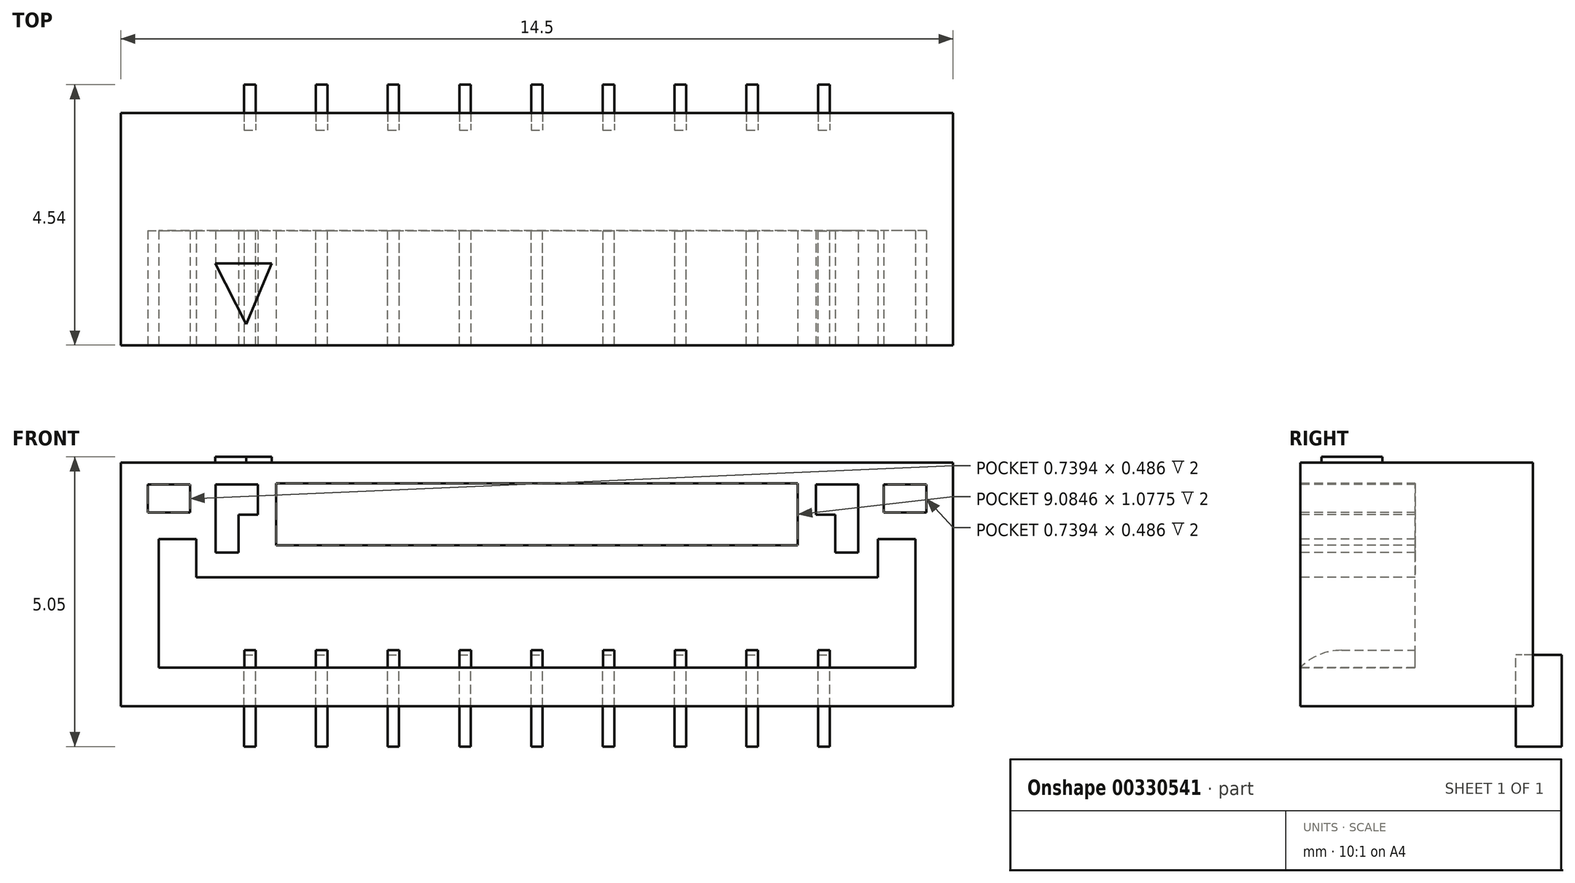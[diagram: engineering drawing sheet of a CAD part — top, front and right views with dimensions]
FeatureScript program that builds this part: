
annotation { "Feature Type Name" : "Feature", "Feature Type Description" : "" }
export const myFeature = defineFeature(function(context is Context, id is Id, definition is map)
    precondition{}
    {
        {
            var Q0;
            Q0=qCreatedBy(makeId("Top.planeOp"),FACE);
            var sketch = newSketch(context, id + "F0", { "sketchPlane" : qUnion([Q0])});
            skLineSegment(sketch, "E0.bottom", {"start": v(7.25, -2.02) * mm, "end": v(-7.25, -2.03) * mm});
            skLineSegment(sketch, "E0.top", {"start": v(7.25, 2.03) * mm, "end": v(-7.25, 2.02) * mm});
            skLineSegment(sketch, "E0.left", {"start": v(7.25, -2.02) * mm, "end": v(7.25, 2.03) * mm});
            skLineSegment(sketch, "E0.right", {"start": v(-7.25, -2.03) * mm, "end": v(-7.25, 2.02) * mm});
            skPoint(sketch, "E0.middle", {"position": v(0, 0) * mm});
            skSolve(sketch);
        }
        {
            var Q0;
            Q0=qSketchRegion(id+"F0",true);
            extrude(context, id + "F1", {"entities" : qUnion([Q0]), "depth" : 4.25 * mm, "offsetDistance" : 25 * mm});
        }
        {
            var Q0;
            Q0=makeQuery(id+"F1.opExtrude","SWEPT_FACE",FACE,{"disambiguationData":[OSD([sQuery(id+"F0.wireOp",EDGE,"E0.bottom")])]});
            var sketch = newSketch(context, id + "F2", { "sketchPlane" : qUnion([Q0])});
            skLineSegment(sketch, "E1", {"start": v(0, 0.68) * mm, "end": v(-6.6, 0.68) * mm});
            skLineSegment(sketch, "E2", {"start": v(-6.6, 0.68) * mm, "end": v(-6.6, 2.92) * mm});
            skLineSegment(sketch, "E3", {"start": v(-6.6, 2.92) * mm, "end": v(-5.94, 2.92) * mm});
            skLineSegment(sketch, "E4", {"start": v(-5.94, 2.92) * mm, "end": v(-5.94, 2.25) * mm});
            skLineSegment(sketch, "E5", {"start": v(-5.94, 0.68) * mm, "end": v(0, 0.68) * mm});
            skLineSegment(sketch, "E6", {"start": v(0, 0.68) * mm, "end": v(0, 0.68) * mm});
            skLineSegment(sketch, "E7.bottom", {"start": v(-6.78, 3.87) * mm, "end": v(-6.04, 3.87) * mm});
            skLineSegment(sketch, "E7.top", {"start": v(-6.78, 3.38) * mm, "end": v(-6.04, 3.38) * mm});
            skLineSegment(sketch, "E7.left", {"start": v(-6.78, 3.87) * mm, "end": v(-6.78, 3.38) * mm});
            skLineSegment(sketch, "E7.right", {"start": v(-6.04, 3.87) * mm, "end": v(-6.04, 3.38) * mm});
            skLineSegment(sketch, "E8.bottom", {"start": v(-4.54, 3.89) * mm, "end": v(0, 3.89) * mm});
            skLineSegment(sketch, "E8.top", {"start": v(-4.54, 2.81) * mm, "end": v(0, 2.81) * mm});
            skLineSegment(sketch, "E8.left", {"start": v(-4.54, 3.89) * mm, "end": v(-4.54, 2.81) * mm});
            skLineSegment(sketch, "E9", {"start": v(-5.6, 3.87) * mm, "end": v(-5.6, 2.68) * mm});
            skLineSegment(sketch, "E10", {"start": v(-5.6, 2.68) * mm, "end": v(-5.2, 2.68) * mm});
            skLineSegment(sketch, "E11", {"start": v(-5.2, 2.68) * mm, "end": v(-5.2, 3.34) * mm});
            skLineSegment(sketch, "E12", {"start": v(-5.2, 3.34) * mm, "end": v(-4.86, 3.34) * mm});
            skLineSegment(sketch, "E13", {"start": v(-4.86, 3.34) * mm, "end": v(-4.86, 3.87) * mm});
            skLineSegment(sketch, "E14", {"start": v(-4.86, 3.87) * mm, "end": v(-5.6, 3.87) * mm});
            skLineSegment(sketch, "E15.MirrorCS", {"start": v(5.94, 2.92) * mm, "end": v(5.94, 2.25) * mm});
            skLineSegment(sketch, "E16.MirrorCS", {"start": v(6.78, 3.87) * mm, "end": v(6.78, 3.38) * mm});
            skLineSegment(sketch, "E17.MirrorCS", {"start": v(6.04, 3.87) * mm, "end": v(6.04, 3.38) * mm});
            skLineSegment(sketch, "E18.MirrorCS", {"start": v(5.2, 3.34) * mm, "end": v(4.86, 3.34) * mm});
            skLineSegment(sketch, "E19.MirrorCS", {"start": v(5.6, 2.68) * mm, "end": v(5.2, 2.68) * mm});
            skLineSegment(sketch, "E20.MirrorCS", {"start": v(4.86, 3.34) * mm, "end": v(4.86, 3.87) * mm});
            skLineSegment(sketch, "E21.MirrorCS", {"start": v(6.78, 3.87) * mm, "end": v(6.04, 3.87) * mm});
            skLineSegment(sketch, "E22.MirrorCS", {"start": v(6.78, 3.38) * mm, "end": v(6.04, 3.38) * mm});
            skLineSegment(sketch, "E23.MirrorCS", {"start": v(5.94, 0.68) * mm, "end": v(0, 0.68) * mm});
            skLineSegment(sketch, "E24.MirrorCS", {"start": v(6.6, 2.92) * mm, "end": v(5.94, 2.92) * mm});
            skLineSegment(sketch, "E25.MirrorCS", {"start": v(6.6, 0.68) * mm, "end": v(6.6, 2.92) * mm});
            skLineSegment(sketch, "E26.MirrorCS", {"start": v(0, 0.68) * mm, "end": v(6.6, 0.68) * mm});
            skLineSegment(sketch, "E27.MirrorCS", {"start": v(5.6, 3.87) * mm, "end": v(5.6, 2.68) * mm});
            skLineSegment(sketch, "E28.MirrorCS", {"start": v(4.54, 3.89) * mm, "end": v(4.54, 2.81) * mm});
            skLineSegment(sketch, "E29.MirrorCS", {"start": v(4.54, 3.89) * mm, "end": v(0, 3.89) * mm});
            skLineSegment(sketch, "E30.MirrorCS", {"start": v(4.54, 2.81) * mm, "end": v(0, 2.81) * mm});
            skLineSegment(sketch, "E31.MirrorCS", {"start": v(4.86, 3.87) * mm, "end": v(5.6, 3.87) * mm});
            skLineSegment(sketch, "E32.MirrorCS", {"start": v(5.2, 2.68) * mm, "end": v(5.2, 3.34) * mm});
            skLineSegment(sketch, "E33", {"start": v(-5.94, 2.25) * mm, "end": v(5.94, 2.25) * mm});
            skSolve(sketch);
        }
        {
            var Q0;
            Q0=qSketchRegion(id+"F2",true);
            extrude(context, id + "F3", {"entities" : qUnion([Q0]), "operationType" : NewBodyOperationType.REMOVE, "oppositeDirection" : true, "depth" : 2 * mm, "offsetDistance" : 25 * mm});
        }
        {
            var Q0;
            Q0=makeQuery(id+"F3.boolean.opBoolean","COPY",FACE,{"derivedFrom":makeQuery(id+"F3.opExtrude","SWEPT_FACE",FACE,{"disambiguationData":[OSD([sQuery(id+"F2.wireOp",EDGE,"E1"),sQuery(id+"F2.wireOp",EDGE,"E5"),sQuery(id+"F2.wireOp",EDGE,"E26.MirrorCS")])]})});
            var sketch = newSketch(context, id + "F4", { "sketchPlane" : qUnion([Q0])});
            skLineSegment(sketch, "E34", {"start": v(0, -1.03) * mm, "end": v(0, -4.7) * mm, "construction": true});
            skPoint(sketch, "E34.endSnap0", {"position": v(0, -2.03) * mm});
            skLineSegment(sketch, "E35.bottom", {"start": v(-1.15, -2.03) * mm, "end": v(-1.35, -2.03) * mm});
            skLineSegment(sketch, "E35.top", {"start": v(-1.15, -0.03) * mm, "end": v(-1.35, -0.03) * mm});
            skLineSegment(sketch, "E35.left", {"start": v(-1.15, -2.03) * mm, "end": v(-1.15, -0.03) * mm});
            skLineSegment(sketch, "E35.right", {"start": v(-1.35, -2.03) * mm, "end": v(-1.35, -0.03) * mm});
            skPoint(sketch, "E35.middle", {"position": v(-1.25, -1.03) * mm});
            skPoint(sketch, "E36.1.0.0", {"position": v(-2.5, -1.03) * mm});
            skLineSegment(sketch, "E36.1.0.1", {"start": v(-2.6, -2.03) * mm, "end": v(-2.6, -0.03) * mm});
            skLineSegment(sketch, "E36.1.0.2", {"start": v(-2.4, -2.03) * mm, "end": v(-2.6, -2.03) * mm});
            skLineSegment(sketch, "E36.1.0.3", {"start": v(-2.4, -2.03) * mm, "end": v(-2.4, -0.03) * mm});
            skLineSegment(sketch, "E36.1.0.4", {"start": v(-2.4, -0.03) * mm, "end": v(-2.6, -0.03) * mm});
            skPoint(sketch, "E36.2.0.0", {"position": v(-3.75, -1.03) * mm});
            skLineSegment(sketch, "E36.2.0.1", {"start": v(-3.85, -2.03) * mm, "end": v(-3.85, -0.03) * mm});
            skLineSegment(sketch, "E36.2.0.2", {"start": v(-3.65, -2.03) * mm, "end": v(-3.85, -2.03) * mm});
            skLineSegment(sketch, "E36.2.0.3", {"start": v(-3.65, -2.03) * mm, "end": v(-3.65, -0.03) * mm});
            skLineSegment(sketch, "E36.2.0.4", {"start": v(-3.65, -0.03) * mm, "end": v(-3.85, -0.03) * mm});
            skPoint(sketch, "E36.3.0.0", {"position": v(-5, -1.03) * mm});
            skLineSegment(sketch, "E36.3.0.1", {"start": v(-5.1, -2.03) * mm, "end": v(-5.1, -0.03) * mm});
            skLineSegment(sketch, "E36.3.0.2", {"start": v(-4.9, -2.03) * mm, "end": v(-5.1, -2.03) * mm});
            skLineSegment(sketch, "E36.3.0.3", {"start": v(-4.9, -2.03) * mm, "end": v(-4.9, -0.03) * mm});
            skLineSegment(sketch, "E36.3.0.4", {"start": v(-4.9, -0.03) * mm, "end": v(-5.1, -0.03) * mm});
            skLineSegment(sketch, "E36.direction1", {"start": v(-1.35, -2.03) * mm, "end": v(-2.6, -2.03) * mm, "construction": true});
            skLineSegment(sketch, "E37.MirrorCS", {"start": v(4.9, -0.03) * mm, "end": v(5.1, -0.03) * mm});
            skLineSegment(sketch, "E38.MirrorCS", {"start": v(1.15, -2.03) * mm, "end": v(1.35, -2.03) * mm});
            skLineSegment(sketch, "E39.MirrorCS", {"start": v(3.65, -0.03) * mm, "end": v(3.85, -0.03) * mm});
            skLineSegment(sketch, "E40.MirrorCS", {"start": v(2.4, -2.03) * mm, "end": v(2.6, -2.03) * mm});
            skPoint(sketch, "E41.MirrorP", {"position": v(3.75, -1.03) * mm});
            skLineSegment(sketch, "E42.MirrorCS", {"start": v(5.1, -2.03) * mm, "end": v(5.1, -0.03) * mm});
            skPoint(sketch, "E43.MirrorP", {"position": v(1.25, -1.03) * mm});
            skLineSegment(sketch, "E44.MirrorCS", {"start": v(4.9, -2.03) * mm, "end": v(5.1, -2.03) * mm});
            skLineSegment(sketch, "E45.MirrorCS", {"start": v(4.9, -2.03) * mm, "end": v(4.9, -0.03) * mm});
            skLineSegment(sketch, "E46.MirrorCS", {"start": v(1.15, -0.03) * mm, "end": v(1.35, -0.03) * mm});
            skLineSegment(sketch, "E47.MirrorCS", {"start": v(1.15, -2.03) * mm, "end": v(1.15, -0.03) * mm});
            skLineSegment(sketch, "E48.MirrorCS", {"start": v(1.35, -2.03) * mm, "end": v(1.35, -0.03) * mm});
            skLineSegment(sketch, "E49.MirrorCS", {"start": v(2.6, -2.03) * mm, "end": v(2.6, -0.03) * mm});
            skLineSegment(sketch, "E50.MirrorCS", {"start": v(2.4, -2.03) * mm, "end": v(2.4, -0.03) * mm});
            skLineSegment(sketch, "E51.MirrorCS", {"start": v(2.4, -0.03) * mm, "end": v(2.6, -0.03) * mm});
            skLineSegment(sketch, "E52.MirrorCS", {"start": v(3.85, -2.03) * mm, "end": v(3.85, -0.03) * mm});
            skLineSegment(sketch, "E53.MirrorCS", {"start": v(3.65, -2.03) * mm, "end": v(3.65, -0.03) * mm});
            skLineSegment(sketch, "E54.MirrorCS", {"start": v(3.65, -2.03) * mm, "end": v(3.85, -2.03) * mm});
            skPoint(sketch, "E55.MirrorP", {"position": v(5, -1.03) * mm});
            skPoint(sketch, "E56.MirrorP", {"position": v(2.5, -1.03) * mm});
            skLineSegment(sketch, "E57.MirrorCS", {"start": v(1.35, -2.03) * mm, "end": v(2.6, -2.03) * mm, "construction": true});
            skLineSegment(sketch, "E58.bottom", {"start": v(0.1, -2.03) * mm, "end": v(-0.1, -2.03) * mm});
            skLineSegment(sketch, "E58.top", {"start": v(0.1, -0.03) * mm, "end": v(-0.1, -0.03) * mm});
            skLineSegment(sketch, "E58.left", {"start": v(0.1, -2.03) * mm, "end": v(0.1, -0.03) * mm});
            skLineSegment(sketch, "E58.right", {"start": v(-0.1, -2.03) * mm, "end": v(-0.1, -0.03) * mm});
            skPoint(sketch, "E58.middle", {"position": v(0, -1.03) * mm});
            skSolve(sketch);
        }
        {
            var Q0;
            Q0=qSketchRegion(id+"F4",true);
            extrude(context, id + "F5", {"entities" : qUnion([Q0]), "depth" : .3 * mm, "offsetDistance" : 25 * mm});
        }
        {
            var Q0;
            Q0=makeQuery(id+"F5.opExtrude","CAP_EDGE",EDGE,{"disambiguationData":[OSD([sQuery(id+"F4.wireOp",EDGE,"E36.3.0.2")])],"isStart":false});
            var Q1;
            Q1=makeQuery(id+"F5.opExtrude","CAP_EDGE",EDGE,{"disambiguationData":[OSD([sQuery(id+"F4.wireOp",EDGE,"E36.2.0.2")])],"isStart":false});
            var Q2;
            Q2=makeQuery(id+"F5.opExtrude","CAP_EDGE",EDGE,{"disambiguationData":[OSD([sQuery(id+"F4.wireOp",EDGE,"E36.1.0.2")])],"isStart":false});
            var Q3;
            Q3=makeQuery(id+"F5.opExtrude","CAP_EDGE",EDGE,{"disambiguationData":[OSD([sQuery(id+"F4.wireOp",EDGE,"E35.bottom")])],"isStart":false});
            var Q4;
            Q4=makeQuery(id+"F5.opExtrude","CAP_EDGE",EDGE,{"disambiguationData":[OSD([sQuery(id+"F4.wireOp",EDGE,"E58.bottom")])],"isStart":false});
            var Q5;
            Q5=makeQuery(id+"F5.opExtrude","CAP_EDGE",EDGE,{"disambiguationData":[OSD([sQuery(id+"F4.wireOp",EDGE,"E38.MirrorCS")])],"isStart":false});
            var Q6;
            Q6=makeQuery(id+"F5.opExtrude","CAP_EDGE",EDGE,{"disambiguationData":[OSD([sQuery(id+"F4.wireOp",EDGE,"E40.MirrorCS")])],"isStart":false});
            var Q7;
            Q7=makeQuery(id+"F5.opExtrude","CAP_EDGE",EDGE,{"disambiguationData":[OSD([sQuery(id+"F4.wireOp",EDGE,"E54.MirrorCS")])],"isStart":false});
            var Q8;
            Q8=makeQuery(id+"F5.opExtrude","CAP_EDGE",EDGE,{"disambiguationData":[OSD([sQuery(id+"F4.wireOp",EDGE,"E44.MirrorCS")])],"isStart":false});
            fillet(context, id + "F6", {"entities" : qUnion([Q0, Q1, Q2, Q3, Q4, Q5, Q6, Q7, Q8]), "radius" : 1 * mm, "tangentPropagation" : true, "allowEdgeOverflow" : false});
        }
        {
            var Q0;
            Q0=makeQuery(id+"F1.opExtrude","CAP_FACE",FACE,{"disambiguationData":[OSD([sQuery(id+"F0.wireOp",EDGE,"E0.bottom"),sQuery(id+"F0.wireOp",EDGE,"E0.top"),sQuery(id+"F0.wireOp",EDGE,"E0.left"),sQuery(id+"F0.wireOp",EDGE,"E0.right")])],"isStart":false});
            var sketch = newSketch(context, id + "F7", { "sketchPlane" : qUnion([Q0])});
            skLineSegment(sketch, "E59", {"start": v(-5.07, -1.66) * mm, "end": v(-4.62, -0.6) * mm});
            skLineSegment(sketch, "E60", {"start": v(-4.62, -0.6) * mm, "end": v(-5.6, -0.6) * mm});
            skLineSegment(sketch, "E61", {"start": v(-5.6, -0.6) * mm, "end": v(-5.07, -1.66) * mm});
            skSolve(sketch);
        }
        {
            var Q0;
            Q0 = qSketchRegion(id + "F7", true);
            extrude(context, id + "F8", {"entities" : qUnion([Q0]), "depth" : .1 * mm, "offsetDistance" : 25 * mm});
        }
        {
            var Q0;
            Q0=makeQuery(id+"F1.opExtrude","SWEPT_FACE",FACE,{"disambiguationData":[OSD([sQuery(id+"F0.wireOp",EDGE,"E0.top")])]});
            var sketch = newSketch(context, id + "F9", { "sketchPlane" : qUnion([Q0])});
            skLineSegment(sketch, "E62.bottom", {"start": v(-4.9, -0.7) * mm, "end": v(-5.1, -0.7) * mm});
            skLineSegment(sketch, "E62.top", {"start": v(-4.9, 0.9) * mm, "end": v(-5.1, 0.9) * mm});
            skLineSegment(sketch, "E62.left", {"start": v(-4.9, -0.7) * mm, "end": v(-4.9, 0.9) * mm});
            skLineSegment(sketch, "E62.right", {"start": v(-5.1, -0.7) * mm, "end": v(-5.1, 0.9) * mm});
            skPoint(sketch, "E62.middle", {"position": v(-5, 0.1) * mm});
            skPoint(sketch, "E63.endSnap0", {"position": v(0, 0.1) * mm});
            skPoint(sketch, "E64.1.0.0", {"position": v(-3.75, 0.1) * mm});
            skLineSegment(sketch, "E64.1.0.1", {"start": v(-3.65, -0.7) * mm, "end": v(-3.65, 0.9) * mm});
            skLineSegment(sketch, "E64.1.0.2", {"start": v(-3.85, -0.7) * mm, "end": v(-3.85, 0.9) * mm});
            skLineSegment(sketch, "E64.1.0.3", {"start": v(-3.65, -0.7) * mm, "end": v(-3.85, -0.7) * mm});
            skLineSegment(sketch, "E64.1.0.4", {"start": v(-3.65, 0.9) * mm, "end": v(-3.85, 0.9) * mm});
            skPoint(sketch, "E64.2.0.0", {"position": v(-2.5, 0.1) * mm});
            skLineSegment(sketch, "E64.2.0.1", {"start": v(-2.4, -0.7) * mm, "end": v(-2.4, 0.9) * mm});
            skLineSegment(sketch, "E64.2.0.2", {"start": v(-2.6, -0.7) * mm, "end": v(-2.6, 0.9) * mm});
            skLineSegment(sketch, "E64.2.0.3", {"start": v(-2.4, -0.7) * mm, "end": v(-2.6, -0.7) * mm});
            skLineSegment(sketch, "E64.2.0.4", {"start": v(-2.4, 0.9) * mm, "end": v(-2.6, 0.9) * mm});
            skPoint(sketch, "E64.3.0.0", {"position": v(-1.25, 0.1) * mm});
            skLineSegment(sketch, "E64.3.0.1", {"start": v(-1.15, -0.7) * mm, "end": v(-1.15, 0.9) * mm});
            skLineSegment(sketch, "E64.3.0.2", {"start": v(-1.35, -0.7) * mm, "end": v(-1.35, 0.9) * mm});
            skLineSegment(sketch, "E64.3.0.3", {"start": v(-1.15, -0.7) * mm, "end": v(-1.35, -0.7) * mm});
            skLineSegment(sketch, "E64.3.0.4", {"start": v(-1.15, 0.9) * mm, "end": v(-1.35, 0.9) * mm});
            skLineSegment(sketch, "E64.4.0.1", {"start": v(0.1, -0.7) * mm, "end": v(0.1, 0.9) * mm});
            skLineSegment(sketch, "E64.4.0.2", {"start": v(-0.1, -0.7) * mm, "end": v(-0.1, 0.9) * mm});
            skLineSegment(sketch, "E64.4.0.3", {"start": v(0.1, -0.7) * mm, "end": v(-0.1, -0.7) * mm});
            skLineSegment(sketch, "E64.4.0.4", {"start": v(0.1, 0.9) * mm, "end": v(-0.1, 0.9) * mm});
            skPoint(sketch, "E64.5.0.0", {"position": v(1.25, 0.1) * mm});
            skLineSegment(sketch, "E64.5.0.1", {"start": v(1.35, -0.7) * mm, "end": v(1.35, 0.9) * mm});
            skLineSegment(sketch, "E64.5.0.2", {"start": v(1.15, -0.7) * mm, "end": v(1.15, 0.9) * mm});
            skLineSegment(sketch, "E64.5.0.3", {"start": v(1.35, -0.7) * mm, "end": v(1.15, -0.7) * mm});
            skLineSegment(sketch, "E64.5.0.4", {"start": v(1.35, 0.9) * mm, "end": v(1.15, 0.9) * mm});
            skPoint(sketch, "E64.6.0.0", {"position": v(2.5, 0.1) * mm});
            skLineSegment(sketch, "E64.6.0.1", {"start": v(2.6, -0.7) * mm, "end": v(2.6, 0.9) * mm});
            skLineSegment(sketch, "E64.6.0.2", {"start": v(2.4, -0.7) * mm, "end": v(2.4, 0.9) * mm});
            skLineSegment(sketch, "E64.6.0.3", {"start": v(2.6, -0.7) * mm, "end": v(2.4, -0.7) * mm});
            skLineSegment(sketch, "E64.6.0.4", {"start": v(2.6, 0.9) * mm, "end": v(2.4, 0.9) * mm});
            skPoint(sketch, "E64.7.0.0", {"position": v(3.75, 0.1) * mm});
            skLineSegment(sketch, "E64.7.0.1", {"start": v(3.85, -0.7) * mm, "end": v(3.85, 0.9) * mm});
            skLineSegment(sketch, "E64.7.0.2", {"start": v(3.65, -0.7) * mm, "end": v(3.65, 0.9) * mm});
            skLineSegment(sketch, "E64.7.0.3", {"start": v(3.85, -0.7) * mm, "end": v(3.65, -0.7) * mm});
            skLineSegment(sketch, "E64.7.0.4", {"start": v(3.85, 0.9) * mm, "end": v(3.65, 0.9) * mm});
            skPoint(sketch, "E64.8.0.0", {"position": v(5, 0.1) * mm});
            skLineSegment(sketch, "E64.8.0.1", {"start": v(5.1, -0.7) * mm, "end": v(5.1, 0.9) * mm});
            skLineSegment(sketch, "E64.8.0.2", {"start": v(4.9, -0.7) * mm, "end": v(4.9, 0.9) * mm});
            skLineSegment(sketch, "E64.8.0.3", {"start": v(5.1, -0.7) * mm, "end": v(4.9, -0.7) * mm});
            skLineSegment(sketch, "E64.8.0.4", {"start": v(5.1, 0.9) * mm, "end": v(4.9, 0.9) * mm});
            skLineSegment(sketch, "E64.direction1", {"start": v(-5.1, -0.7) * mm, "end": v(-3.85, -0.7) * mm, "construction": true});
            skLineSegment(sketch, "E65", {"start": v(0, 4.25) * mm, "end": v(0, -2.19) * mm, "construction": true});
            skSolve(sketch);
        }
        {
            var Q0;
            Q0 = qSketchRegion(id + "F9", true);
            extrude(context, id + "F10", {"entities" : qUnion([Q0]), "depth" : .5 * mm, "offsetDistance" : 25 * mm, "hasSecondDirection" : true, "secondDirectionOppositeDirection" : true, "secondDirectionDepth" : .3 * mm});
        }
    });
